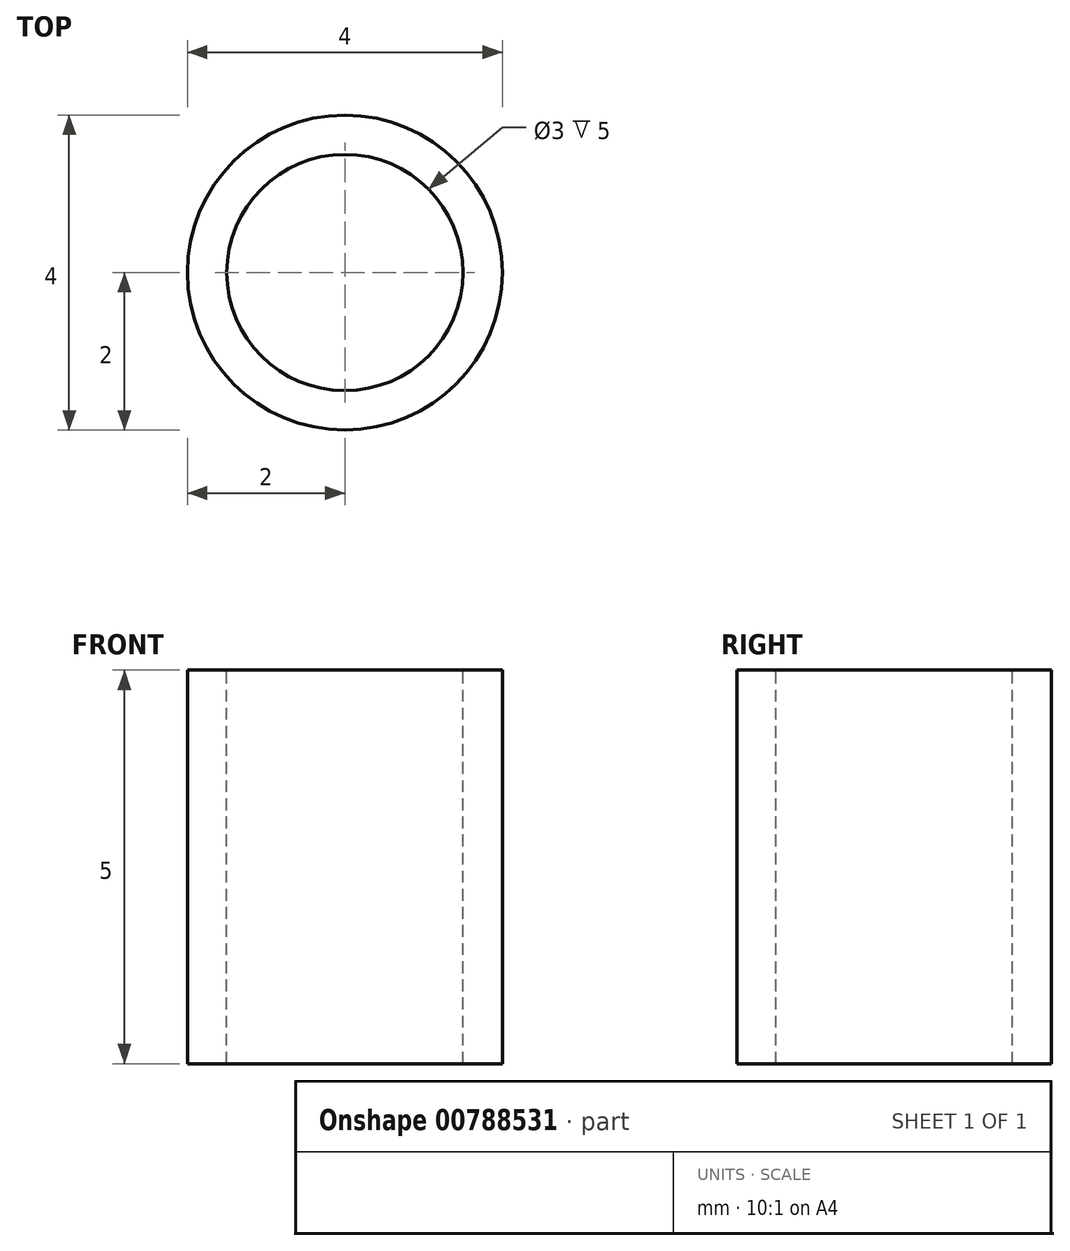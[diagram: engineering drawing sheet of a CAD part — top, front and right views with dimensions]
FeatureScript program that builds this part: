
annotation { "Feature Type Name" : "Feature", "Feature Type Description" : "" }
export const myFeature = defineFeature(function(context is Context, id is Id, definition is map)
    precondition{}
    {
        {
            var Q0;
            Q0=qCreatedBy(makeId("Front.planeOp"),FACE);
            var sketch = newSketch(context, id + "F0", { "sketchPlane" : qUnion([Q0])});
            skLineSegment(sketch, "E0.bottom", {"start": v(-2, 0) * mm, "end": v(-1.5, 0) * mm});
            skLineSegment(sketch, "E0.top", {"start": v(-2, 5) * mm, "end": v(-1.5, 5) * mm});
            skLineSegment(sketch, "E0.left", {"start": v(-2, 0) * mm, "end": v(-2, 5) * mm});
            skLineSegment(sketch, "E0.right", {"start": v(-1.5, 0) * mm, "end": v(-1.5, 5) * mm});
            skLineSegment(sketch, "E1", {"start": v(0, 7.06) * mm, "end": v(0, -6.6) * mm});
            skSolve(sketch);
        }
        {
            var Q0;
            Q0=makeQuery(id+"F0.imprint","IMPRINT",FACE,{"disambiguationData":[TD([[makeQuery(id+"F0.imprint","IMPRINT",EDGE,{"derivedFrom":sQuery(id+"F0.wireOp",EDGE,"E0.bottom")}),1.0]])]});
            var Q1;
            Q1=sQuery(id+"F0.wireOp",EDGE,"E1");
            revolve(context, id + "F1", {"surfaceOperationType" : NewSurfaceOperationType.NEW, "entities" : qUnion([Q0]), "axis" : qUnion([Q1]), "revolveType" : RevolveType.FULL});
        }
    });
